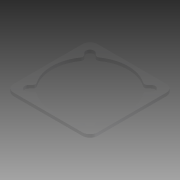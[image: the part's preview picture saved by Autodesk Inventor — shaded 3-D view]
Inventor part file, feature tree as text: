
AUTODESK INVENTOR PART (.ipt)
format: ipt  version: 2015 (Build 190159000, 159)  size: 126,464 bytes
history: native  units: mm
features: extrude x1, fillet x1
ambient origin geometry x8: Origin, YZ Plane, XZ Plane, XY Plane, X Axis, Y Axis, Z Axis, Center Point
bodies: Solid1 (feature_tree)
feature tree (2):
  extrude  "Extrusión1"  Depth=50.0mm
  fillet  "Empalme1"  Radius=55.0mm
